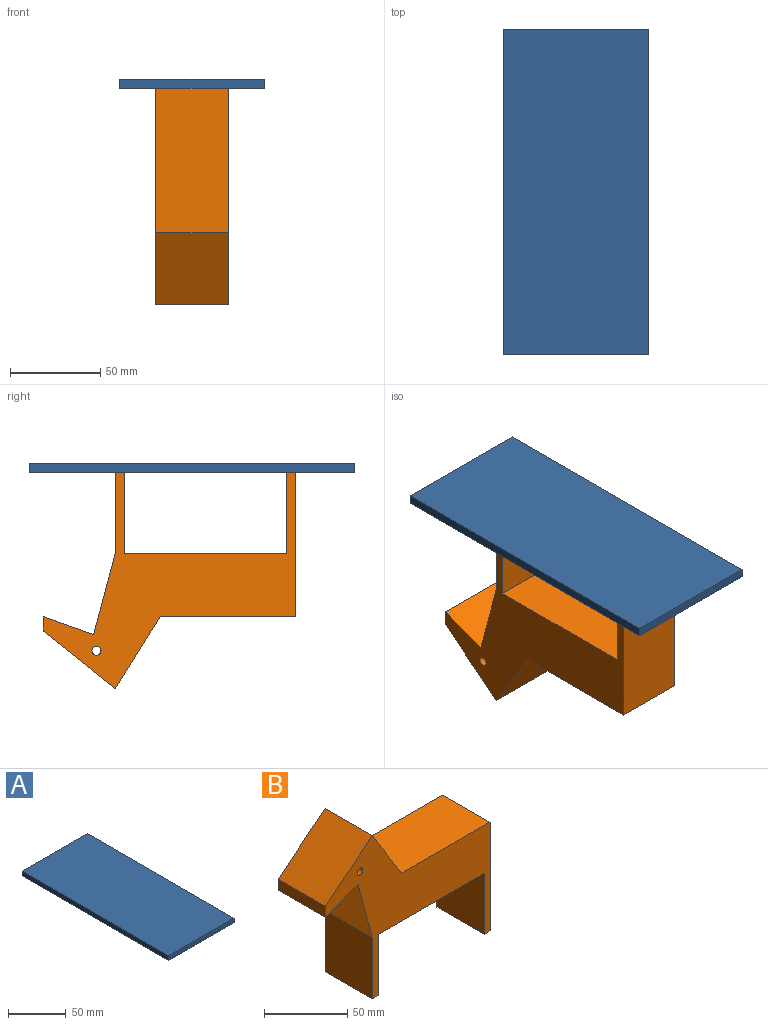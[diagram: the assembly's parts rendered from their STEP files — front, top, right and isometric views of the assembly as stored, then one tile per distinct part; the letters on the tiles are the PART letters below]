
ASSEMBLY  parts=2 mates=1
PART A: 6 faces, bbox 80x180x5 mm
  f0: plane 180x5mm, normal (-1,0,0), area 900mm2, adj f1,f3,f4,f5
  f1: plane 80x5mm, normal (0,-1,0), area 400mm2, adj f0,f2,f4,f5
  f2: plane 180x5mm, normal (1,0,0), area 900mm2, adj f1,f3,f4,f5
  f3: plane 80x5mm, normal (0,1,0), area 400mm2, adj f0,f2,f4,f5
  f4: plane 180x80mm, normal (0,0,-1), area 14400mm2, adj f0,f1,f2,f3
  f5: plane 180x80mm, normal (0,0,1), area 14400mm2, adj f0,f1,f2,f3
PART B: 16 faces, bbox 140x40x120 mm
  f0: plane 80x40mm, normal (1,0,0), area 3200mm2, adj f1,f12,f13,f14
  f1: plane 75x40mm, normal (0,0,1), area 3000mm2, adj f0,f2,f13,f14
  f2: plane 40x40mm, normal (0.85,0,0.53), area 1886.8mm2, adj f1,f3,f13,f14
  f3: plane 40x40mm, normal (-0.62,0,0.78), area 2049mm2, adj f2,f4,f13,f14
  f4: plane 40x8mm, normal (-1,0,0), area 320mm2, adj f3,f5,f13,f14
  f5: plane 40x28mm, normal (0.34,0,-0.94), area 1189.3mm2, adj f4,f6,f13,f14
  f6: plane 45x40mm, normal (-0.97,0,-0.26), area 1862.9mm2, adj f5,f7,f13,f14
  f7: plane 45x40mm, normal (-1,0,0), area 1800mm2, adj f6,f8,f13,f14
  f8: plane 40x5mm, normal (0,0,-1), area 200mm2, adj f7,f9,f13,f14
  f9: plane 45x40mm, normal (1,0,0), area 1800mm2, adj f8,f10,f13,f14
  f10: plane 90x40mm, normal (0,0,-1), area 3600mm2, adj f9,f11,f13,f14
  f11: plane 45x40mm, normal (-1,0,0), area 1800mm2, adj f10,f12,f13,f14
  f12: plane 40x5mm, normal (0,0,-1), area 200mm2, adj f0,f11,f13,f14
  f13: plane 140x120mm, normal (0,-1,0), area 5400.4mm2, adj f0,f1,f2,f3,f4,f5,f6,f7
  f14: plane 140x120mm, normal (0,1,0), area 5400.4mm2, adj f0,f1,f2,f3,f4,f5,f6,f7
  f15: cylinder r=2.5mm len=40mm, axis (0,-1,0), area 628.3mm2, adj f13,f14
PLACE A rot(axis=(0,0,1),180deg) t=(282.26,10,0)mm
PLACE B rot(axis=(0.71,-0.71,0),180deg) t=(20,-147.5,-5)mm
MATE parallel A.f4 <-> B.f8  axis (0,0,-1) through (40,-90,-5)mm
